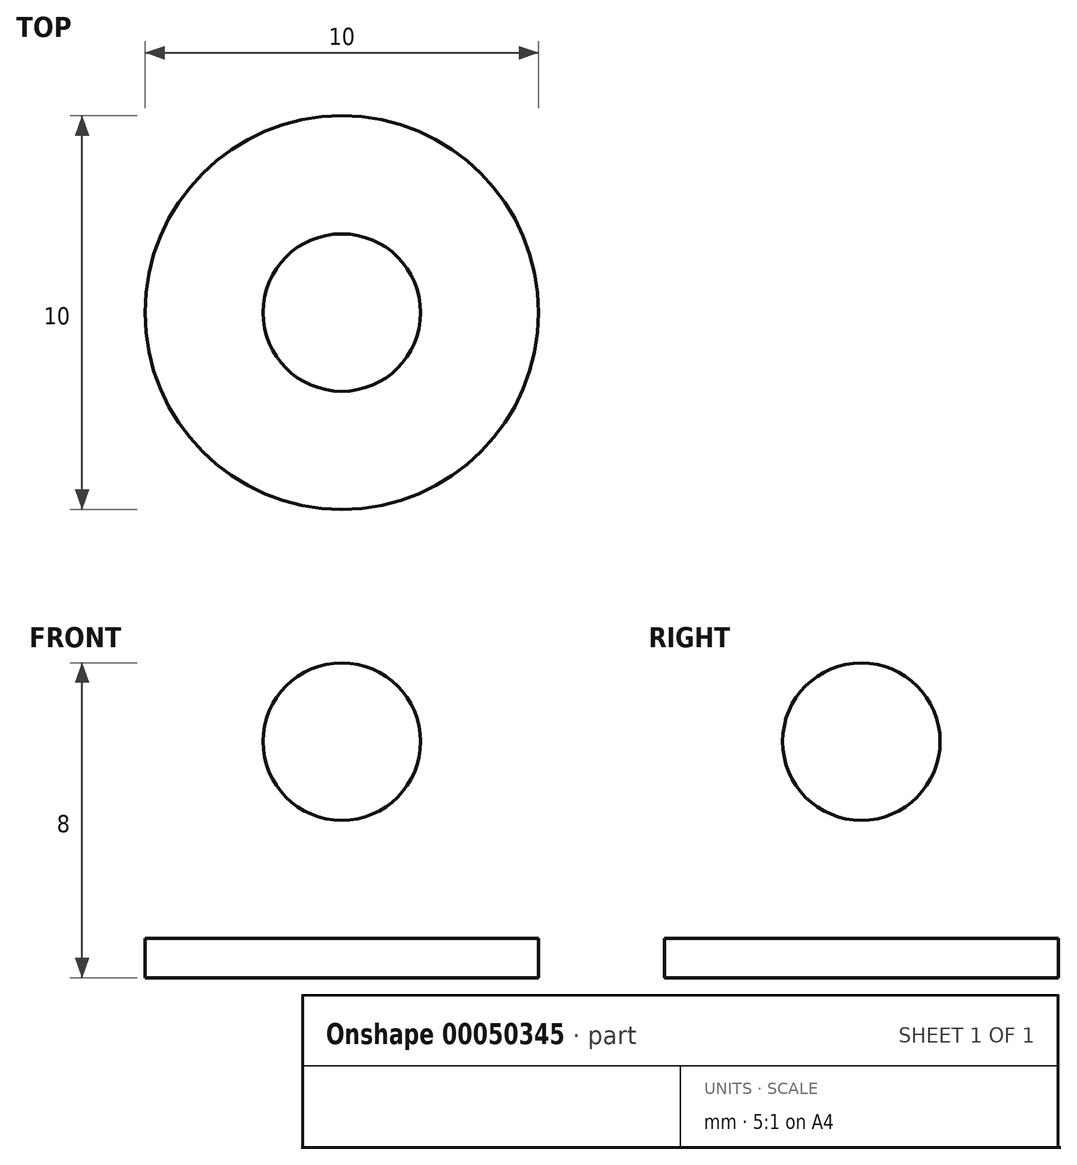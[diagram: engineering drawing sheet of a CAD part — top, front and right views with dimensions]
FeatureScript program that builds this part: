
annotation { "Feature Type Name" : "Feature", "Feature Type Description" : "" }
export const myFeature = defineFeature(function(context is Context, id is Id, definition is map)
    precondition{}
    {
        {
            var Q0;
            Q0=qCreatedBy(makeId("Front.planeOp"),FACE);
            var sketch = newSketch(context, id + "F0", { "sketchPlane" : qUnion([Q0])});
            skArc(sketch, "E0", {"start": v(0, -2) * mm, "mid": v(2, 0) * mm, "end": v(0, 2) * mm});
            skLineSegment(sketch, "E1", {"start": v(0, 2) * mm, "end": v(0, -2) * mm});
            skLineSegment(sketch, "E2.bottom", {"start": v(0, -5) * mm, "end": v(5, -5) * mm});
            skLineSegment(sketch, "E2.top", {"start": v(0, -6) * mm, "end": v(5, -6) * mm});
            skLineSegment(sketch, "E2.left", {"start": v(0, -5) * mm, "end": v(0, -6) * mm});
            skLineSegment(sketch, "E2.right", {"start": v(5, -5) * mm, "end": v(5, -6) * mm});
            skSolve(sketch);
        }
        {
            var Q0;
            Q0=makeQuery(id+"F0.imprint","IMPRINT",FACE,{"disambiguationData":[TD([[makeQuery(id+"F0.imprint","IMPRINT",EDGE,{"derivedFrom":sQuery(id+"F0.wireOp",EDGE,"E0")}),1.0]])]});
            var Q1;
            Q1=makeQuery(id+"F0.imprint","IMPRINT",FACE,{"disambiguationData":[TD([[makeQuery(id+"F0.imprint","IMPRINT",EDGE,{"derivedFrom":sQuery(id+"F0.wireOp",EDGE,"E2.bottom")}),-1.0]])]});
            var Q2;
            Q2=sQuery(id+"F0.wireOp",EDGE,"E1");
            revolve(context, id + "F1", {"entities" : qUnion([Q0, Q1]), "axis" : qUnion([Q2]), "revolveType" : RevolveType.FULL});
        }
    });
